# Revit family: WasteSet-ForBasins-Vitra-ArkitektaSeries-A45137
name_source: partatom
category: Plumbing Fixtures
revit_build: Autodesk Revit 2017 (Build: 20160225_1515(x64)
units: mm (PartAtom-declared; Revit-internal decimal feet)

## family parameters
Always vertical = No
Cut with Voids When Loaded = No
OmniClass Number = 23.45.00.00
OmniClass Title = Sanitary, Laundry, and Cleaning Equipment
Part Type = Normal
Room Calculation Point = No
Round Connector Dimension = Use Diameter
Shared = Yes
Work Plane-Based = Yes

## types (1)
- WasteSet-ForBasins-Vitra-ArkitektaSeries-A45137
    Article No. (default) = A45137
    BIMobject category = Sanitary - Taps & Mixers
    Brand = VitrA
    CW Connection = No
    Coating Material = Chrome (Metal)
    Color = Chrome
    Default Elevation = 600 mm
    Description = Waste Sets Waste Set
    Design country = Turkey
    HW Connection = No
    Hot Water Supply (max.) = 80 °C
    Hot Water temperature, factory set to = 38 °C
    IFC Classification = Sanitary Terminal
    Main Material = Metal
    Manufacturer = Vitra
    Manufacturer name = Vitra
    Masterformat 2014 Code = 22 13 16
    Masterformat 2014 Description = Sanitary Waste and Vent Piping
    Min. flow pressure of = 0.5 bar
    Model = A45137
    NBS Referans Code = 31-76
    NBS Referans Description = Sanitary Dispensing And Disposal Units
    Nominal Depth (mm) = 70 mm  [stored 0.229659 ft]
    Nominal Height (mm) = 70 mm  [stored 0.229659 ft]
    Nominal Width (mm) = 70 mm  [stored 0.229659 ft]
    OmniClass Code = 23-21 23 27
    OmniClass Description = Residential Waste Disposal Units
    Product SKU = A45137
    Product Type = Washbasin Siphon Set
    Product certification = https://www.vitraglobal.com
    Product family = Waste Set
    Product group = Waste Set
    Product url = https://www.vitraglobal.com
    Range of Hot Water Supply = 5 - 65 °C
    Range of flow pressure = 1 - 5 bar
    Technical description = https://www.vitraglobal.com
    Test Pressure = 16 bar
    UNSPSC Description = Sanitary ware
    URL = https://vitraglobal.com
    Uniclass 1.4 Code = L7218
    Uniclass 1.4 Description = Sanitary disposal units
    Uniclass 2.0 Code = PR-31-76
    Uniclass 2.0 Description = Sanitary Dispensing And Disposal Units
    Uniclass 2015 Code = Pr_60_45_90
    Uniclass 2015 Name = Wastewater and water mixer products
    Uniformat II Code = D2010
    Uniformat II Description = Plumbing Fixtures
    Vent Connection = No
    Warranty Period (Year) = 5
    Waste Connection = Yes
    Youtube = https://www.youtube.com

note: [stored X ft] marks values corroborated as IEEE doubles in the binary element streams (Revit-internal decimal feet)

## geometry (parser evidence)
native form markers: Sweep x3
no freeform markers — native parametric forms only
